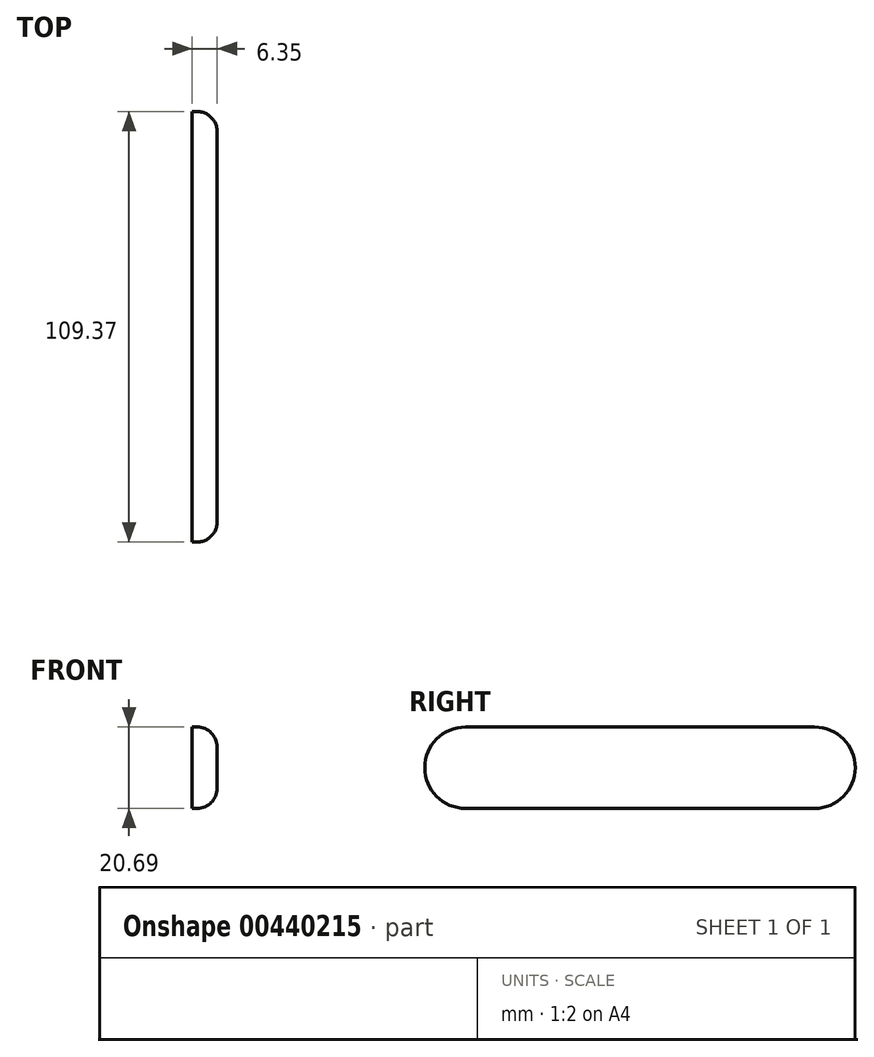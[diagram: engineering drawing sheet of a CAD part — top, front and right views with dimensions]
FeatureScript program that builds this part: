
annotation { "Feature Type Name" : "Feature", "Feature Type Description" : "" }
export const myFeature = defineFeature(function(context is Context, id is Id, definition is map)
    precondition{}
    {
        {
            var Q0;
            Q0=qCreatedBy(makeId("Right.planeOp"),FACE);
            var sketch = newSketch(context, id + "F0", { "sketchPlane" : qUnion([Q0])});
            skLineSegment(sketch, "E0.bottom", {"start": v(-44.54, 10.25) * mm, "end": v(44.14, 10.25) * mm});
            skLineSegment(sketch, "E0.top", {"start": v(-44.54, -10.44) * mm, "end": v(44.14, -10.44) * mm});
            skLineSegment(sketch, "E0.left", {"start": v(-44.54, 10.25) * mm, "end": v(-44.54, -10.44) * mm});
            skLineSegment(sketch, "E0.right", {"start": v(44.14, 10.25) * mm, "end": v(44.14, -10.44) * mm});
            skCircle(sketch, "E1", {"center": v(-44.54, -0.1) * mm, "radius": 10.35 * mm});
            skCircle(sketch, "E2", {"center": v(44.14, -0.1) * mm, "radius": 10.35 * mm});
            skSolve(sketch);
        }
        {
            var Q0;
            {var subQ0=sQuery(id+"F0.wireOp",EDGE,"E0.left");Q0=makeQuery(id+"F0.imprint","IMPRINT",FACE,{"disambiguationData":[TD([[makeQuery(id+"F0.imprint","IMPRINT",EDGE,{"derivedFrom":subQ0}),-1.0]])]});}
            var Q1;
            {var subQ0=sQuery(id+"F0.wireOp",EDGE,"E0.left");Q1=makeQuery(id+"F0.imprint","IMPRINT",FACE,{"disambiguationData":[TD([[makeQuery(id+"F0.imprint","IMPRINT",EDGE,{"derivedFrom":subQ0}),1.0]])]});}
            var Q2;
            {var subQ0=sQuery(id+"F0.wireOp",EDGE,"E0.right");Q2=makeQuery(id+"F0.imprint","IMPRINT",FACE,{"disambiguationData":[TD([[makeQuery(id+"F0.imprint","IMPRINT",EDGE,{"derivedFrom":subQ0}),1.0]])]});}
            var Q3;
            {var subQ0=sQuery(id+"F0.wireOp",EDGE,"E0.right");Q3=makeQuery(id+"F0.imprint","IMPRINT",FACE,{"disambiguationData":[TD([[makeQuery(id+"F0.imprint","IMPRINT",EDGE,{"derivedFrom":subQ0}),-1.0]])]});}
            var Q4;
            {var subQ0=sQuery(id+"F0.wireOp",EDGE,"E0.bottom");Q4=makeQuery(id+"F0.imprint","IMPRINT",FACE,{"disambiguationData":[TD([[makeQuery(id+"F0.imprint","IMPRINT",EDGE,{"derivedFrom":subQ0}),-1.0]])]});}
            extrude(context, id + "F1", {"entities" : qUnion([Q0, Q1, Q2, Q3, Q4]), "depth" : 6.35 * mm});
        }
        {
            var Q0;
            Q0=makeQuery(id+"F1.opExtrude","CAP_FACE",FACE,{"disambiguationData":[OSD([sQuery(id+"F0.wireOp",EDGE,"E0.bottom"),sQuery(id+"F0.wireOp",EDGE,"E0.top"),sQuery(id+"F0.wireOp",EDGE,"E1"),sQuery(id+"F0.wireOp",EDGE,"E2")])],"isStart":false});
            fillet(context, id + "F2", {"entities" : qUnion([Q0]), "radius" : 5.08 * mm, "tangentPropagation" : true, "allowEdgeOverflow" : false});
        }
    });
